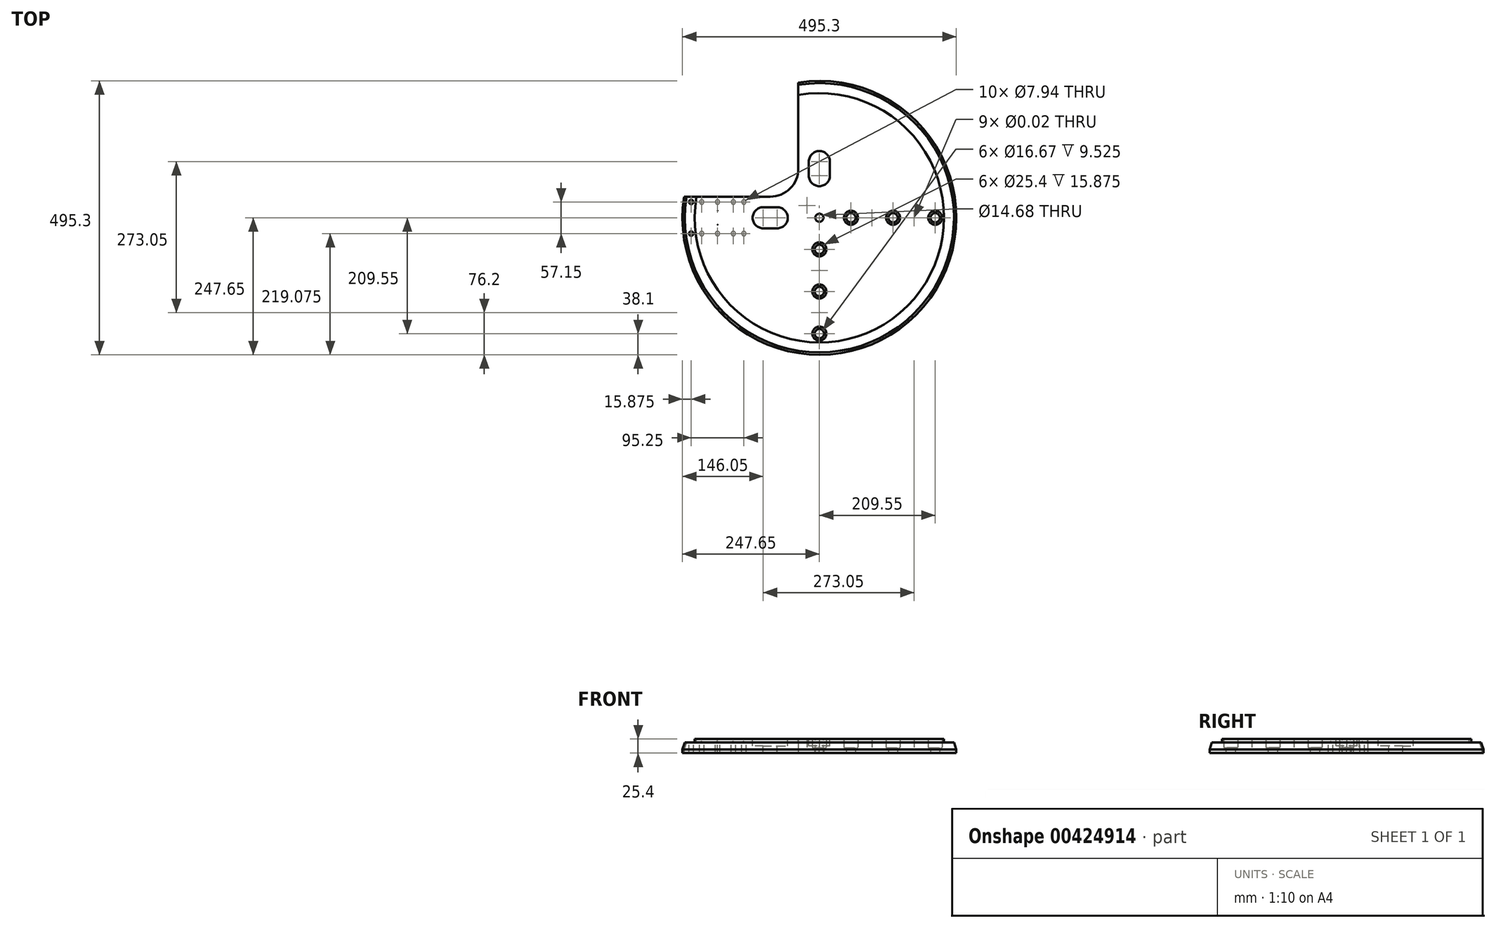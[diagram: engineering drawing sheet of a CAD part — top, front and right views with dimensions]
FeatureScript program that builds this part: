
annotation { "Feature Type Name" : "Feature", "Feature Type Description" : "" }
export const myFeature = defineFeature(function(context is Context, id is Id, definition is map)
    precondition{}
    {
        {
            var Q0;
            Q0=qCreatedBy(makeId("Front.planeOp"),FACE);
            var sketch = newSketch(context, id + "F0", { "sketchPlane" : qUnion([Q0])});
            skLineSegment(sketch, "E0", {"start": v(0, 0) * mm, "end": v(247.65, 0) * mm});
            skLineSegment(sketch, "E1", {"start": v(247.65, 0) * mm, "end": v(247.65, 6.35) * mm});
            skLineSegment(sketch, "E2", {"start": v(247.65, 6.35) * mm, "end": v(241.3, 25.4) * mm});
            skLineSegment(sketch, "E3", {"start": v(241.3, 25.4) * mm, "end": v(0, 25.4) * mm});
            skLineSegment(sketch, "E4", {"start": v(0, 25.4) * mm, "end": v(0, 0) * mm});
            skSolve(sketch);
        }
        {
            var Q0;
            Q0 = qSketchRegion(id + "F0", true);
            var Q1;
            Q1=sQuery(id+"F0.wireOp",EDGE,"E4");
            revolve(context, id + "F1", {"entities" : qUnion([Q0]), "axis" : qUnion([Q1]), "revolveType" : RevolveType.FULL});
        }
        {
            var Q0;
            Q0=makeQuery(id+"F1.opRevolve","SWEPT_FACE",FACE,{"disambiguationData":[OSD([sQuery(id+"F0.wireOp",EDGE,"E0")])]});
            var sketch = newSketch(context, id + "F2", { "sketchPlane" : qUnion([Q0])});
            skLineSegment(sketch, "E5", {"start": v(0, 0) * mm, "end": v(-247.65, 0) * mm, "construction": true});
            skLineSegment(sketch, "E6", {"start": v(-184.15, 28.57) * mm, "end": v(-184.15, -28.58) * mm, "construction": true});
            skPoint(sketch, "E7", {"position": v(-184.15, -12.7) * mm});
            skPoint(sketch, "E8", {"position": v(-184.15, 12.7) * mm});
            skSolve(sketch);
        }
        {
            var Q0;
            Q0=sQuery(id+"F2.wireOp",VERTEX,"E7");
            var Q1;
            Q1=sQuery(id+"F2.wireOp",VERTEX,"E8");
            var Q2;
            Q2=makeQuery(id+"F1.opRevolve","SWEPT_BODY",BODY,{"disambiguationData":[OSD([sQuery(id+"F0.wireOp",EDGE,"E0"),sQuery(id+"F0.wireOp",EDGE,"E1"),sQuery(id+"F0.wireOp",EDGE,"E2"),sQuery(id+"F0.wireOp",EDGE,"E3"),sQuery(id+"F0.wireOp",EDGE,"E4")])]});
            hole(context, id + "F3", {"style" : HoleStyle.SIMPLE, "endStyle" : HoleEndStyle.THROUGH, "standardTappedOrClearance" : lookupTablePath({ "standard" : "ANSI", "size" : "3/8 (0.38)", "type" : "Drilled" }), "standardBlindInLast" : lookupTablePath({ "standard" : "ANSI", "size" : "3/8", "type" : "Drilled" }), "holeDiameter" : 3 / 203.2 * mm, "isTappedThrough" : true, "tappedDepth" : 19.54 * mm, "tapClearance" : 3, "locations" : qUnion([Q0, Q1]), "scope" : qUnion([Q2]), "startStyle" : HoleStartStyle.SKETCH});
        }
        {
            var Q0;
            Q0=makeQuery(id+"F1.opRevolve","SWEPT_FACE",FACE,{"disambiguationData":[OSD([sQuery(id+"F0.wireOp",EDGE,"E0")])]});
            var sketch = newSketch(context, id + "F4", { "sketchPlane" : qUnion([Q0])});
            skLineSegment(sketch, "E9", {"start": v(0, 0) * mm, "end": v(-247.65, 0) * mm, "construction": true});
            skLineSegment(sketch, "E10", {"start": v(0, 0) * mm, "end": v(0, -247.65) * mm, "construction": true});
            skLineSegment(sketch, "E11.0", {"start": v(-38.1, -88.9) * mm, "end": v(-38.1, -244.7) * mm});
            skLineSegment(sketch, "E12.0", {"start": v(-88.9, -38.1) * mm, "end": v(-244.7, -38.1) * mm});
            skPoint(sketch, "E13.visualSharp", {"position": v(-38.1, -38.1) * mm});
            skArc(sketch, "E13.filletArc", {"start": v(-38.1, -88.9) * mm, "mid": v(-52.98, -52.98) * mm, "end": v(-88.9, -38.1) * mm});
            skArc(sketch, "E14.0", {"start": v(-244.7, -38.1) * mm, "mid": v(-175.11, -175.11) * mm, "end": v(-38.1, -244.7) * mm});
            skSolve(sketch);
        }
        {
            var Q0;
            Q0 = qSketchRegion(id + "F4", true);
            extrude(context, id + "F5", {"entities" : qUnion([Q0]), "operationType" : NewBodyOperationType.REMOVE, "endBound" : BoundingType.THROUGH_ALL, "oppositeDirection" : true, "depth" : 25.4 * mm});
        }
        {
            var Q0;
            Q0=makeQuery(id+"F1.opRevolve","SWEPT_FACE",FACE,{"disambiguationData":[OSD([sQuery(id+"F0.wireOp",EDGE,"E0")])]});
            var sketch = newSketch(context, id + "F6", { "sketchPlane" : qUnion([Q0])});
            skLineSegment(sketch, "E15", {"start": v(-247.65, 0) * mm, "end": v(0, 0) * mm, "construction": true});
            skLineSegment(sketch, "E16", {"start": v(-231.78, -28.58) * mm, "end": v(-136.53, -28.57) * mm, "construction": true});
            skLineSegment(sketch, "E17", {"start": v(-184.15, 12.7) * mm, "end": v(-184.15, -38.1) * mm, "construction": true});
            skPoint(sketch, "E18", {"position": v(-212.72, -28.58) * mm});
            skPoint(sketch, "E19", {"position": v(-184.15, -28.58) * mm});
            skPoint(sketch, "E20", {"position": v(-155.58, -28.58) * mm});
            skPoint(sketch, "E21", {"position": v(-136.53, -28.57) * mm});
            skPoint(sketch, "E22", {"position": v(-231.78, -28.58) * mm});
            skPoint(sketch, "E23.MirrorP", {"position": v(-136.53, 28.57) * mm});
            skPoint(sketch, "E24.MirrorP", {"position": v(-155.58, 28.57) * mm});
            skPoint(sketch, "E25.MirrorP", {"position": v(-184.15, 28.57) * mm});
            skPoint(sketch, "E26.MirrorP", {"position": v(-212.73, 28.57) * mm});
            skPoint(sketch, "E27.MirrorP", {"position": v(-231.78, 28.57) * mm});
            skSolve(sketch);
        }
        {
            var Q0;
            Q0=sQuery(id+"F6.wireOp",VERTEX,"E19");
            var Q1;
            Q1=sQuery(id+"F6.wireOp",VERTEX,"E20");
            var Q2;
            Q2=sQuery(id+"F6.wireOp",VERTEX,"E21");
            var Q3;
            Q3=sQuery(id+"F6.wireOp",VERTEX,"E18");
            var Q4;
            Q4=sQuery(id+"F6.wireOp",VERTEX,"E22");
            var Q5;
            Q5=sQuery(id+"F6.wireOp",VERTEX,"E27.MirrorP");
            var Q6;
            Q6=sQuery(id+"F6.wireOp",VERTEX,"E26.MirrorP");
            var Q7;
            Q7=sQuery(id+"F6.wireOp",VERTEX,"E25.MirrorP");
            var Q8;
            Q8=sQuery(id+"F6.wireOp",VERTEX,"E24.MirrorP");
            var Q9;
            Q9=sQuery(id+"F6.wireOp",VERTEX,"E23.MirrorP");
            var Q10;
            Q10=makeQuery(id+"F1.opRevolve","SWEPT_BODY",BODY,{"disambiguationData":[OSD([sQuery(id+"F0.wireOp",EDGE,"E0"),sQuery(id+"F0.wireOp",EDGE,"E1"),sQuery(id+"F0.wireOp",EDGE,"E2"),sQuery(id+"F0.wireOp",EDGE,"E3"),sQuery(id+"F0.wireOp",EDGE,"E4")])]});
            hole(context, id + "F7", {"style" : HoleStyle.SIMPLE, "endStyle" : HoleEndStyle.BLIND, "standardTappedOrClearance" : lookupTablePath({ "standard" : "ANSI", "engagement" : "75%", "pitch" : "16 tpi", "size" : "3/8", "type" : "Tapped" }), "standardBlindInLast" : lookupTablePath({ "standard" : "ANSI", "engagement" : "75%", "pitch" : "16 tpi", "size" : "3/8", "type" : "Tapped" }), "holeDiameter" : 7.94 * mm, "showTappedDepth" : true, "holeDepth" : 19.05 * mm, "isTappedThrough" : true, "tappedDepth" : 14.29 * mm, "tapClearance" : 3, "locations" : qUnion([Q0, Q1, Q2, Q3, Q4, Q5, Q6, Q7, Q8, Q9]), "scope" : qUnion([Q10]), "majorDiameter" : 9.53 * mm, "startStyle" : HoleStartStyle.SKETCH});
        }
        {
            var Q0;
            Q0=makeQuery(id+"F1.opRevolve","SWEPT_FACE",FACE,{"disambiguationData":[OSD([sQuery(id+"F0.wireOp",EDGE,"E3")])]});
            var sketch = newSketch(context, id + "F8", { "sketchPlane" : qUnion([Q0])});
            skLineSegment(sketch, "E28", {"start": v(0, -241.3) * mm, "end": v(0, 0) * mm, "construction": true});
            skLineSegment(sketch, "E29", {"start": v(0, 0) * mm, "end": v(241.3, 0) * mm, "construction": true});
            skPoint(sketch, "E30", {"position": v(0, -57.15) * mm});
            skPoint(sketch, "E31", {"position": v(0, -133.35) * mm});
            skPoint(sketch, "E32", {"position": v(0, -209.55) * mm});
            skPoint(sketch, "E33", {"position": v(57.15, 0) * mm});
            skPoint(sketch, "E34", {"position": v(133.35, 0) * mm});
            skPoint(sketch, "E35", {"position": v(209.55, 0) * mm});
            skPoint(sketch, "E36", {"position": v(95.25, 0) * mm});
            skPoint(sketch, "E37", {"position": v(171.45, 0) * mm});
            skPoint(sketch, "E38", {"position": v(0, -95.25) * mm});
            skPoint(sketch, "E39", {"position": v(0, -171.45) * mm});
            skSolve(sketch);
        }
        {
            var Q0;
            Q0=sQuery(id+"F8.wireOp",VERTEX,"E33");
            var Q1;
            Q1=sQuery(id+"F8.wireOp",VERTEX,"E34");
            var Q2;
            Q2=sQuery(id+"F8.wireOp",VERTEX,"E35");
            var Q3;
            Q3=sQuery(id+"F8.wireOp",VERTEX,"E30");
            var Q4;
            Q4=sQuery(id+"F8.wireOp",VERTEX,"E31");
            var Q5;
            Q5=sQuery(id+"F8.wireOp",VERTEX,"E32");
            var Q6;
            Q6=makeQuery(id+"F1.opRevolve","SWEPT_BODY",BODY,{"disambiguationData":[OSD([sQuery(id+"F0.wireOp",EDGE,"E0"),sQuery(id+"F0.wireOp",EDGE,"E1"),sQuery(id+"F0.wireOp",EDGE,"E2"),sQuery(id+"F0.wireOp",EDGE,"E3"),sQuery(id+"F0.wireOp",EDGE,"E4")])]});
            hole(context, id + "F9", {"style" : HoleStyle.C_BORE, "endStyle" : HoleEndStyle.THROUGH, "standardTappedOrClearance" : lookupTablePath({ "standard" : "ANSI", "fit" : "Normal (ASME)", "size" : "5/8", "type" : "Clearance" }), "standardBlindInLast" : lookupTablePath({ "fit" : "Free", "standard" : "ANSI", "size" : "5/8", "type" : "Clearance" }), "holeDiameter" : 16.67 * mm, "cBoreDiameter" : 25.4 * mm, "cBoreDepth" : 15.88 * mm, "isTappedThrough" : true, "tappedDepth" : 14.29 * mm, "tapClearance" : 3, "locations" : qUnion([Q0, Q1, Q2, Q3, Q4, Q5]), "scope" : qUnion([Q6]), "startStyle" : HoleStartStyle.SKETCH});
        }
        {
            var Q0;
            Q0=makeQuery(id+"F1.opRevolve","SWEPT_FACE",FACE,{"disambiguationData":[OSD([sQuery(id+"F0.wireOp",EDGE,"E0")])]});
            var sketch = newSketch(context, id + "F10", { "sketchPlane" : qUnion([Q0])});
            skLineSegment(sketch, "E40", {"start": v(0, 0) * mm, "end": v(-247.65, 0) * mm, "construction": true});
            skLineSegment(sketch, "E41", {"start": v(0, 0) * mm, "end": v(0, -247.65) * mm, "construction": true});
            skPoint(sketch, "E42", {"position": v(-76.2, 0) * mm});
            skPoint(sketch, "E43", {"position": v(-101.6, 0) * mm});
            skPoint(sketch, "E44", {"position": v(0, -76.2) * mm});
            skPoint(sketch, "E45", {"position": v(0, -101.6) * mm});
            skSolve(sketch);
        }
        {
            var Q0;
            Q0=sQuery(id+"F10.wireOp",VERTEX,"E42");
            var Q1;
            Q1=sQuery(id+"F10.wireOp",VERTEX,"E43");
            var Q2;
            Q2=sQuery(id+"F10.wireOp",VERTEX,"E44");
            var Q3;
            Q3=sQuery(id+"F10.wireOp",VERTEX,"E45");
            var Q4;
            Q4=makeQuery(id+"F1.opRevolve","SWEPT_BODY",BODY,{"disambiguationData":[OSD([sQuery(id+"F0.wireOp",EDGE,"E0"),sQuery(id+"F0.wireOp",EDGE,"E1"),sQuery(id+"F0.wireOp",EDGE,"E2"),sQuery(id+"F0.wireOp",EDGE,"E3"),sQuery(id+"F0.wireOp",EDGE,"E4")])]});
            hole(context, id + "F11", {"style" : HoleStyle.SIMPLE, "endStyle" : HoleEndStyle.THROUGH, "standardTappedOrClearance" : lookupTablePath({ "standard" : "ANSI", "size" : "9/16 (0.56)", "type" : "Drilled" }), "standardBlindInLast" : lookupTablePath({ "standard" : "ANSI", "size" : "9/16", "type" : "Drilled" }), "holeDiameter" : 9 / 406.4 * mm, "isTappedThrough" : true, "tappedDepth" : 14.3 * mm, "tapClearance" : 3, "locations" : qUnion([Q0, Q1, Q2, Q3]), "scope" : qUnion([Q4]), "startStyle" : HoleStartStyle.SKETCH});
        }
        {
            var Q0;
            Q0=sQuery(id+"F8.wireOp",VERTEX,"E36");
            var Q1;
            Q1=sQuery(id+"F8.wireOp",VERTEX,"E37");
            var Q2;
            Q2=sQuery(id+"F8.wireOp",VERTEX,"E38");
            var Q3;
            Q3=sQuery(id+"F8.wireOp",VERTEX,"E39");
            var Q4;
            Q4=makeQuery(id+"F1.opRevolve","SWEPT_BODY",BODY,{"disambiguationData":[OSD([sQuery(id+"F0.wireOp",EDGE,"E0"),sQuery(id+"F0.wireOp",EDGE,"E1"),sQuery(id+"F0.wireOp",EDGE,"E2"),sQuery(id+"F0.wireOp",EDGE,"E3"),sQuery(id+"F0.wireOp",EDGE,"E4")])]});
            hole(context, id + "F12", {"style" : HoleStyle.SIMPLE, "endStyle" : HoleEndStyle.THROUGH, "standardTappedOrClearance" : lookupTablePath({ "standard" : "ANSI", "size" : "1/2 (0.5)", "type" : "Drilled" }), "standardBlindInLast" : lookupTablePath({ "standard" : "ANSI", "size" : "1/2", "type" : "Drilled" }), "holeDiameter" : 1 / 50.8 * mm, "isTappedThrough" : true, "tappedDepth" : 14.3 * mm, "tapClearance" : 3, "locations" : qUnion([Q0, Q1, Q2, Q3]), "scope" : qUnion([Q4]), "startStyle" : HoleStartStyle.SKETCH});
        }
        {
            var Q0;
            Q0=makeQuery(id+"F1.opRevolve","SWEPT_FACE",FACE,{"disambiguationData":[OSD([sQuery(id+"F0.wireOp",EDGE,"E3")])]});
            var sketch = newSketch(context, id + "F13", { "sketchPlane" : qUnion([Q0])});
            skLineSegment(sketch, "E46", {"start": v(-101.6, 0) * mm, "end": v(-76.2, 0) * mm, "construction": true});
            skLineSegment(sketch, "E47", {"start": v(0, 101.6) * mm, "end": v(0, 76.2) * mm, "construction": true});
            skArc(sketch, "E48.0.startCap", {"start": v(-101.6, -19.05) * mm, "mid": v(-120.65, 0) * mm, "end": v(-101.6, 19.05) * mm});
            skArc(sketch, "E48.0.endCap", {"start": v(-76.2, 19.05) * mm, "mid": v(-57.15, 0) * mm, "end": v(-76.2, -19.05) * mm});
            skLineSegment(sketch, "E48.0.left", {"start": v(-101.6, 19.05) * mm, "end": v(-76.2, 19.05) * mm});
            skLineSegment(sketch, "E48.0.right", {"start": v(-101.6, -19.05) * mm, "end": v(-76.2, -19.05) * mm});
            skArc(sketch, "E49.0.startCap", {"start": v(-19.05, 101.6) * mm, "mid": v(0, 120.65) * mm, "end": v(19.05, 101.6) * mm});
            skArc(sketch, "E49.0.endCap", {"start": v(19.05, 76.2) * mm, "mid": v(0, 57.15) * mm, "end": v(-19.05, 76.2) * mm});
            skLineSegment(sketch, "E49.0.left", {"start": v(19.05, 101.6) * mm, "end": v(19.05, 76.2) * mm});
            skLineSegment(sketch, "E49.0.right", {"start": v(-19.05, 101.6) * mm, "end": v(-19.05, 76.2) * mm});
            skSolve(sketch);
        }
        {
            var Q0;
            Q0 = qSketchRegion(id + "F13", true);
            extrude(context, id + "F14", {"entities" : qUnion([Q0]), "operationType" : NewBodyOperationType.REMOVE, "oppositeDirection" : true, "depth" : 12.7 * mm});
        }
        {
            var Q0;
            Q0=makeQuery(id+"F1.opRevolve","SWEPT_FACE",FACE,{"disambiguationData":[OSD([sQuery(id+"F0.wireOp",EDGE,"E3")])]});
            var sketch = newSketch(context, id + "F15", { "sketchPlane" : qUnion([Q0])});
            skCircle(sketch, "E50", {"center": v(0, 0) * mm, "radius": 225.43 * mm});
            skCircle(sketch, "E51", {"center": v(0, 0) * mm, "radius": 263.53 * mm});
            skSolve(sketch);
        }
        {
            var Q0;
            Q0 = qSketchRegion(id + "F15", true);
            extrude(context, id + "F16", {"entities" : qUnion([Q0]), "operationType" : NewBodyOperationType.REMOVE, "oppositeDirection" : true, "depth" : 6.35 * mm});
        }
        {
            var Q0;
            Q0=sQuery(id+"F10.wireOp",VERTEX,"E40.start");
            var Q1;
            Q1=makeQuery(id+"F1.opRevolve","SWEPT_BODY",BODY,{"disambiguationData":[OSD([sQuery(id+"F0.wireOp",EDGE,"E0"),sQuery(id+"F0.wireOp",EDGE,"E1"),sQuery(id+"F0.wireOp",EDGE,"E2"),sQuery(id+"F0.wireOp",EDGE,"E3"),sQuery(id+"F0.wireOp",EDGE,"E4")])]});
            hole(context, id + "F17", {"style" : HoleStyle.SIMPLE, "endStyle" : HoleEndStyle.THROUGH, "standardTappedOrClearance" : lookupTablePath({ "standard" : "ANSI", "engagement" : "75%", "pitch" : "18 tpi", "size" : "5/8", "type" : "Tapped" }), "standardBlindInLast" : lookupTablePath({ "standard" : "ANSI", "engagement" : "75%", "pitch" : "18 tpi", "size" : "5/8", "type" : "Tapped" }), "holeDiameter" : 14.68 * mm, "showTappedDepth" : true, "isTappedThrough" : true, "tappedDepth" : 14.3 * mm, "tapClearance" : 3, "locations" : qUnion([Q0]), "scope" : qUnion([Q1]), "majorDiameter" : 15.88 * mm, "startStyle" : HoleStartStyle.SKETCH});
        }
        {
            var Q0;
            Q0=makeQuery(id+"F1.opRevolve","SWEPT_FACE",FACE,{"disambiguationData":[OSD([sQuery(id+"F0.wireOp",EDGE,"E3")])]});
            var sketch = newSketch(context, id + "F18", { "sketchPlane" : qUnion([Q0])});
            skCircle(sketch, "E52", {"center": v(0, 0) * mm, "radius": 31.75 * mm, "construction": true});
            skLineSegment(sketch, "E53", {"start": v(0, 0) * mm, "end": v(-52.98, 52.98) * mm, "construction": true});
            skLineSegment(sketch, "E54", {"start": v(0, 0) * mm, "end": v(-225.43, 0) * mm, "construction": true});
            skPoint(sketch, "E55", {"position": v(-22.45, 22.45) * mm});
            skSolve(sketch);
        }
        {
            var Q0;
            Q0=sQuery(id+"F18.wireOp",VERTEX,"E55");
            var Q1;
            Q1=makeQuery(id+"F1.opRevolve","SWEPT_BODY",BODY,{"disambiguationData":[OSD([sQuery(id+"F0.wireOp",EDGE,"E0"),sQuery(id+"F0.wireOp",EDGE,"E1"),sQuery(id+"F0.wireOp",EDGE,"E2"),sQuery(id+"F0.wireOp",EDGE,"E3"),sQuery(id+"F0.wireOp",EDGE,"E4")])]});
            hole(context, id + "F19", {"style" : HoleStyle.SIMPLE, "endStyle" : HoleEndStyle.THROUGH, "standardTappedOrClearance" : lookupTablePath({ "standard" : "ANSI", "size" : "1/2 (0.5)", "type" : "Drilled" }), "standardBlindInLast" : lookupTablePath({ "standard" : "ANSI", "size" : "1/2", "type" : "Drilled" }), "holeDiameter" : 1 / 50.8 * mm, "isTappedThrough" : true, "tappedDepth" : 14.3 * mm, "tapClearance" : 3, "locations" : qUnion([Q0]), "scope" : qUnion([Q1]), "startStyle" : HoleStartStyle.SKETCH});
        }
    });
